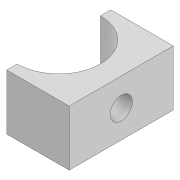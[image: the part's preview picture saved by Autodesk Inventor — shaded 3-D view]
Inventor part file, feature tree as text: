
AUTODESK INVENTOR PART (.ipt)
format: ipt  version: 2022 (Build 260153000, 153)  size: 102,912 bytes
history: native  units: mm
features: extrude x2, sketch x2
ambient origin geometry x8: Origin, YZ Plane, XZ Plane, XY Plane, X Axis, Y Axis, Z Axis, Center Point
bodies: Solid1 (feature_tree)
feature tree (4):
  extrude  "Extrusion1"  Depth=9.0mm TaperAngle=0.0deg
  extrude  "Extrusion2"  Depth=6.0mm
  sketch  "Sketch1"  dims[d1=9.0mm d2=8.0mm d3=0.0mm]
  sketch  "Sketch2"  dims[d4=3.2mm d5=4.0mm d6=7.5mm d7=15.0mm d8=15.0mm d9=12.0mm d10=6.0mm d11=0.0mm]
